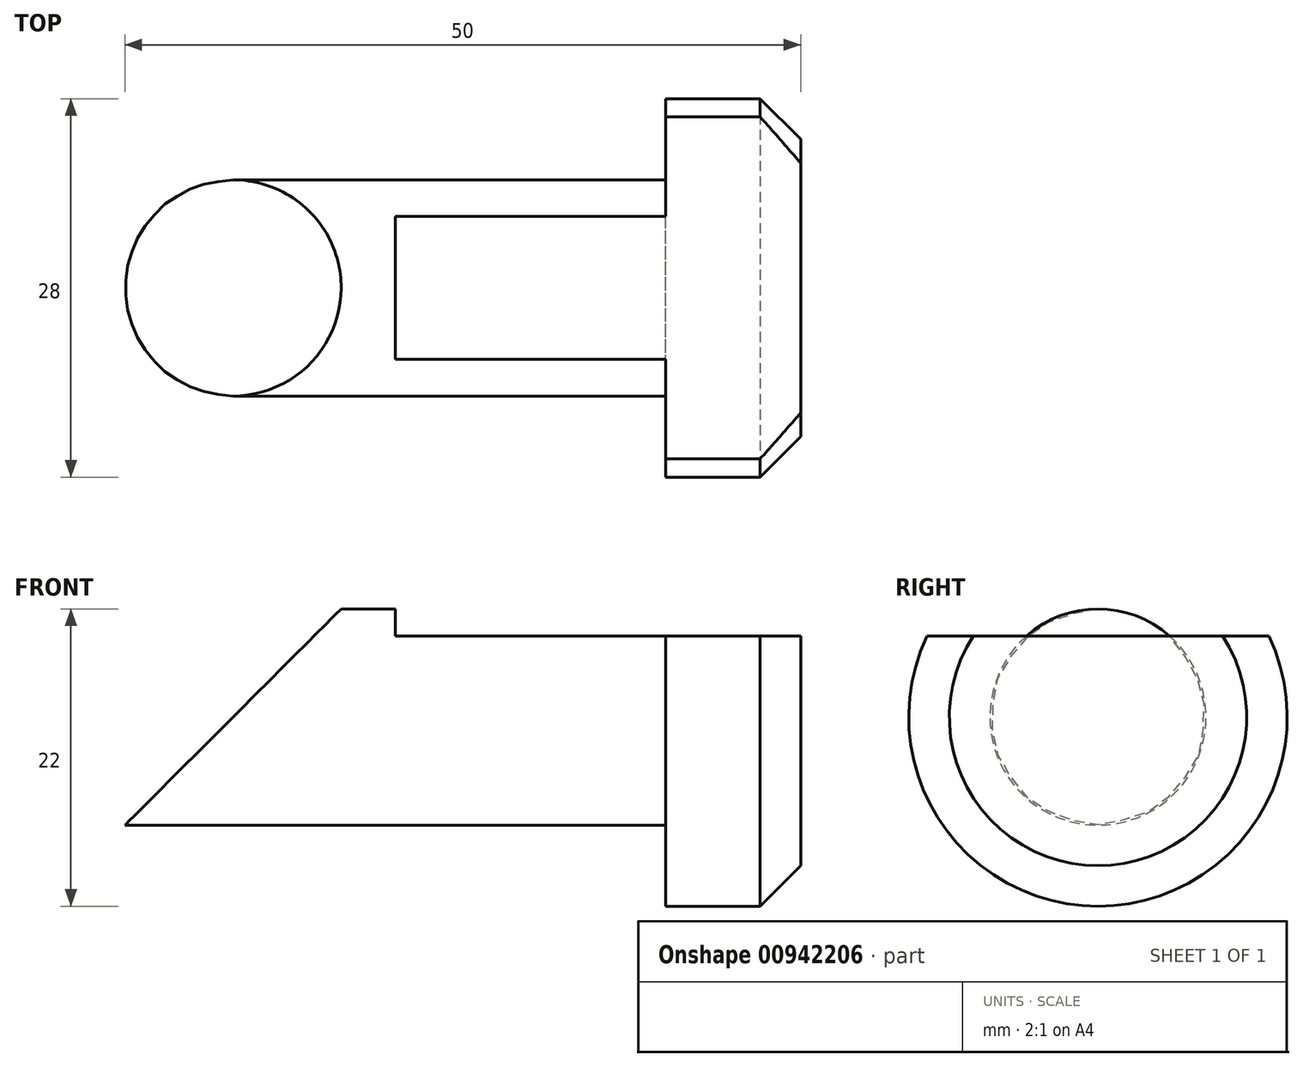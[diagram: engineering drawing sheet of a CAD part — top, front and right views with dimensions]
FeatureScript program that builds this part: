
annotation { "Feature Type Name" : "Feature", "Feature Type Description" : "" }
export const myFeature = defineFeature(function(context is Context, id is Id, definition is map)
    precondition{}
    {
        {
            var Q0;
            Q0=qCreatedBy(makeId("Front.planeOp"),FACE);
            var sketch = newSketch(context, id + "F0", { "sketchPlane" : qUnion([Q0])});
            skLineSegment(sketch, "E0", {"start": v(0, 0) * mm, "end": v(-46.17, 0) * mm, "construction": true});
            skLineSegment(sketch, "E1", {"start": v(-40, 0) * mm, "end": v(-40, 8) * mm});
            skLineSegment(sketch, "E2", {"start": v(-40, 8) * mm, "end": v(0, 8) * mm});
            skLineSegment(sketch, "E3", {"start": v(0, 8) * mm, "end": v(0, 14) * mm});
            skLineSegment(sketch, "E4", {"start": v(0, 14) * mm, "end": v(10, 14) * mm});
            skLineSegment(sketch, "E5", {"start": v(10, 14) * mm, "end": v(10, 0) * mm});
            skLineSegment(sketch, "E6", {"start": v(10, 0) * mm, "end": v(-40, 0) * mm});
            skSolve(sketch);
        }
        {
            var Q0;
            Q0 = qSketchRegion(id + "F0", true);
            var Q1;
            Q1=sQuery(id+"F0.wireOp",EDGE,"E0");
            revolve(context, id + "F1", {"surfaceOperationType" : NewSurfaceOperationType.NEW, "entities" : qUnion([Q0]), "axis" : qUnion([Q1]), "revolveType" : RevolveType.FULL});
        }
        {
            var Q0;
            Q0=makeQuery(id+"F1.opRevolve","SWEPT_EDGE",EDGE,{"disambiguationData":[OSD([sQuery(id+"F0.wireOp",EDGE,"E4"),sQuery(id+"F0.wireOp",EDGE,"E5")])]});
            chamfer(context, id + "F2", {"entities" : qUnion([Q0]), "width" : 3 * mm, "tangentPropagation" : true});
        }
        {
            var Q0;
            Q0=qCreatedBy(makeId("Front.planeOp"),FACE);
            var sketch = newSketch(context, id + "F3", { "sketchPlane" : qUnion([Q0])});
            skLineSegment(sketch, "E7", {"start": v(-20, 16.33) * mm, "end": v(-20, 6) * mm});
            skLineSegment(sketch, "E8", {"start": v(-20, 6) * mm, "end": v(10, 6) * mm});
            skLineSegment(sketch, "E9", {"start": v(10, 6) * mm, "end": v(10, 16.33) * mm});
            skLineSegment(sketch, "E10", {"start": v(10, 16.33) * mm, "end": v(-20, 16.33) * mm});
            skLineSegment(sketch, "E11", {"start": v(-40, 8) * mm, "end": v(13.61, 8) * mm});
            skPoint(sketch, "E12", {"position": v(-40, 8) * mm});
            skSolve(sketch);
        }
        {
            var Q0;
            Q0 = qSketchRegion(id + "F3", true);
            extrude(context, id + "F4", {"entities" : qUnion([Q0]), "operationType" : NewBodyOperationType.REMOVE, "endBound" : BoundingType.SYMMETRIC, "depth" : 30 * mm, "offsetDistance" : 25 * mm});
        }
        {
            var Q0;
            Q0=qCreatedBy(makeId("Front.planeOp"),FACE);
            var sketch = newSketch(context, id + "F5", { "sketchPlane" : qUnion([Q0])});
            skLineSegment(sketch, "E13.top", {"start": v(-40, 8) * mm, "end": v(-24, 8) * mm});
            skLineSegment(sketch, "E13.left", {"start": v(-40, -8) * mm, "end": v(-40, 8) * mm});
            skPoint(sketch, "E13.middle", {"position": v(-24, 0) * mm});
            skLineSegment(sketch, "E14", {"start": v(-40, -8) * mm, "end": v(-24, 8) * mm});
            skPoint(sketch, "E13.right.end.orphan", {"position": v(-8, 8) * mm});
            skSolve(sketch);
        }
        {
            var Q0;
            Q0 = qSketchRegion(id + "F5", true);
            extrude(context, id + "F6", {"entities" : qUnion([Q0]), "operationType" : NewBodyOperationType.REMOVE, "endBound" : BoundingType.SYMMETRIC, "oppositeDirection" : true, "depth" : 30 * mm, "offsetDistance" : 25 * mm});
        }
    });
